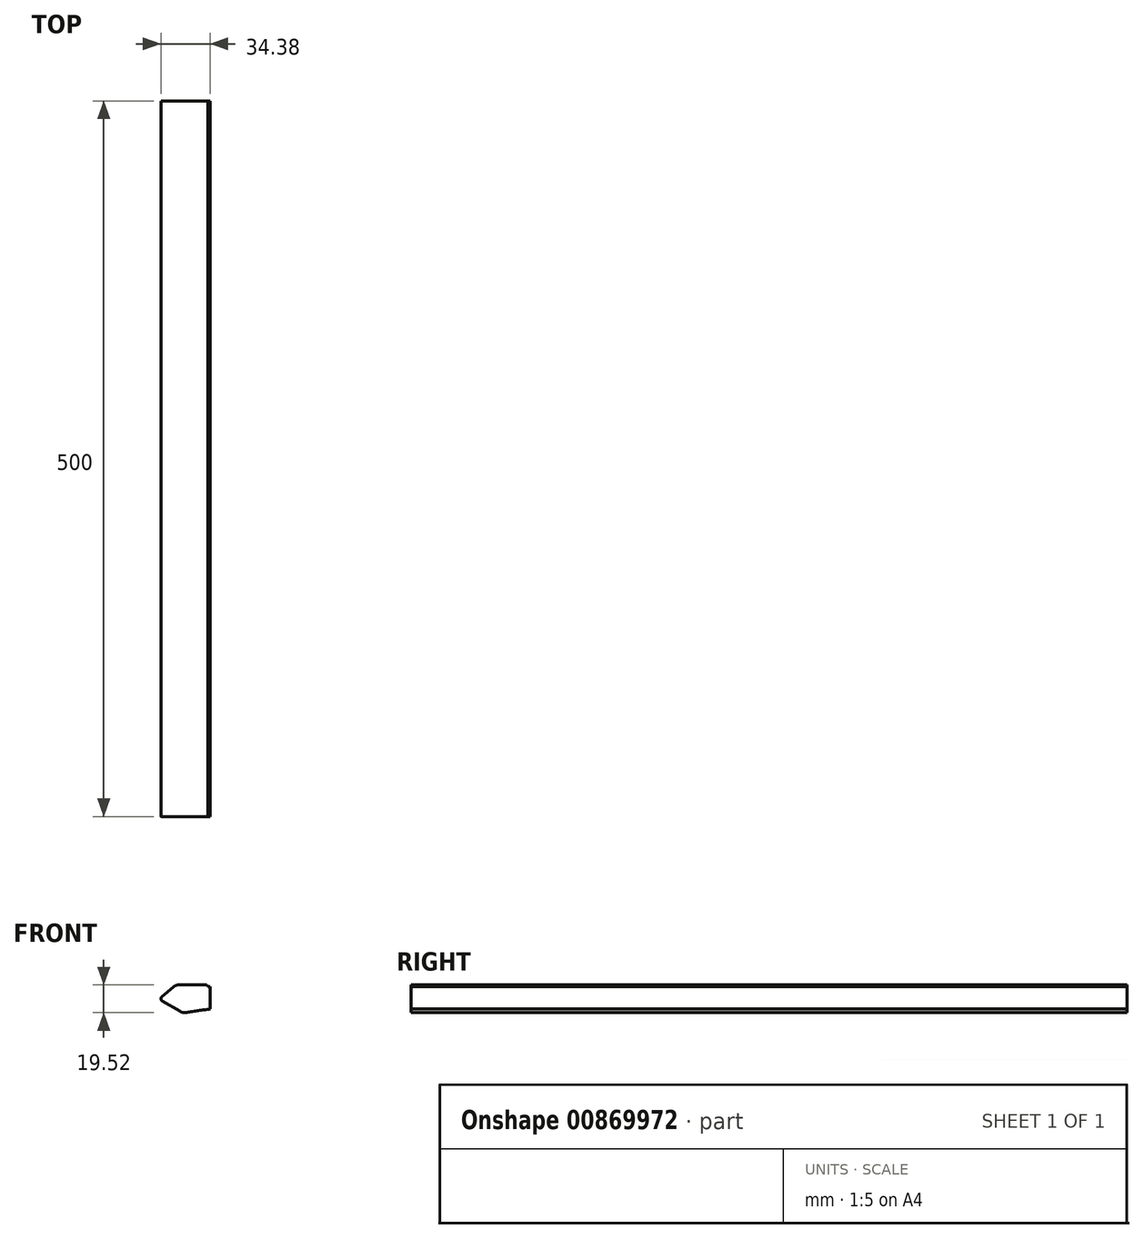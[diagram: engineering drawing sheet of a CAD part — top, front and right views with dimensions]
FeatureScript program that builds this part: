
annotation { "Feature Type Name" : "Feature", "Feature Type Description" : "" }
export const myFeature = defineFeature(function(context is Context, id is Id, definition is map)
    precondition{}
    {
        {
            var Q0;
            Q0=qCreatedBy(makeId("Front.planeOp"),FACE);
            var sketch = newSketch(context, id + "F0", { "sketchPlane" : qUnion([Q0])});
            skLineSegment(sketch, "E0", {"start": v(0, 48.22) * mm, "end": v(0, -32.48) * mm, "construction": true});
            skLineSegment(sketch, "E1", {"start": v(0, 0) * mm, "end": v(22.5, 0) * mm});
            skLineSegment(sketch, "E2", {"start": v(22.5, 0) * mm, "end": v(22.5, 1.3) * mm});
            skLineSegment(sketch, "E3", {"start": v(22.5, 1.3) * mm, "end": v(45.58, 1.3) * mm});
            skLineSegment(sketch, "E4", {"start": v(45.58, 1.3) * mm, "end": v(57.5, -8.7) * mm});
            skLineSegment(sketch, "E5", {"start": v(57.5, -8.7) * mm, "end": v(57.5, -12.7) * mm});
            skLineSegment(sketch, "E6", {"start": v(57.5, -12.7) * mm, "end": v(40.18, -22.7) * mm});
            skLineSegment(sketch, "E7.MirrorCS", {"start": v(0, 0) * mm, "end": v(-22.5, 0) * mm});
            skLineSegment(sketch, "E8.MirrorCS", {"start": v(-22.5, 0) * mm, "end": v(-22.5, 1.3) * mm});
            skLineSegment(sketch, "E9.MirrorCS", {"start": v(-22.5, 1.3) * mm, "end": v(-45.58, 1.3) * mm});
            skLineSegment(sketch, "E10.MirrorCS", {"start": v(-45.58, 1.3) * mm, "end": v(-57.5, -8.7) * mm});
            skLineSegment(sketch, "E11.MirrorCS", {"start": v(-57.5, -8.7) * mm, "end": v(-57.5, -12.7) * mm});
            skLineSegment(sketch, "E12.MirrorCS", {"start": v(-57.5, -12.7) * mm, "end": v(-40.18, -22.7) * mm});
            skArc(sketch, "E13", {"start": v(40.18, -22.7) * mm, "mid": v(0, -18.62) * mm, "end": v(-40.18, -22.7) * mm});
            skSolve(sketch);
        }
        {
            var Q0;
            Q0=makeQuery(id+"F0.imprint","IMPRINT",FACE,{"disambiguationData":[TD([[makeQuery(id+"F0.imprint","IMPRINT",EDGE,{"derivedFrom":sQuery(id+"F0.wireOp",EDGE,"E1")}),-1.0]])]});
            extrude(context, id + "F1", {"entities" : qUnion([Q0]), "endBound" : BoundingType.SYMMETRIC, "depth" : 500 * mm, "offsetDistance" : 25 * mm});
        }
        {
            var Q0;
            Q0=qCreatedBy(makeId("Front.planeOp"),FACE);
            var sketch = newSketch(context, id + "F2", { "sketchPlane" : qUnion([Q0])});
            skLineSegment(sketch, "E14.bottom", {"start": v(-19, -2) * mm, "end": v(19, -2) * mm});
            skLineSegment(sketch, "E14.top", {"start": v(-19, -15) * mm, "end": v(19, -15) * mm});
            skLineSegment(sketch, "E14.left", {"start": v(-19, -2) * mm, "end": v(-19, -15) * mm});
            skLineSegment(sketch, "E14.right", {"start": v(19, -2) * mm, "end": v(19, -15) * mm});
            skSolve(sketch);
        }
        {
            var Q0;
            Q0=qSketchRegion(id+"F2",true);
            extrude(context, id + "F3", {"entities" : qUnion([Q0]), "operationType" : NewBodyOperationType.REMOVE, "endBound" : BoundingType.SYMMETRIC, "oppositeDirection" : true, "depth" : 500 * mm, "offsetDistance" : 25 * mm});
        }
        {
            var Q0;
            Q0=makeQuery(id+"F1.opExtrude","SWEPT_EDGE",EDGE,{"disambiguationData":[OSD([sQuery(id+"F0.wireOp",EDGE,"E2"),sQuery(id+"F0.wireOp",EDGE,"E3")])]});
            var Q1;
            Q1=makeQuery(id+"F1.opExtrude","SWEPT_EDGE",EDGE,{"disambiguationData":[OSD([sQuery(id+"F0.wireOp",EDGE,"E8.MirrorCS"),sQuery(id+"F0.wireOp",EDGE,"E9.MirrorCS")])]});
            fillet(context, id + "F4", {"entities" : qUnion([Q0, Q1]), "radius" : 2 * mm, "tangentPropagation" : true, "allowEdgeOverflow" : false});
        }
        {
            var Q0;
            Q0=makeQuery(id+"F1.opExtrude","SWEPT_EDGE",EDGE,{"disambiguationData":[OSD([sQuery(id+"F0.wireOp",EDGE,"E3"),sQuery(id+"F0.wireOp",EDGE,"E4")])]});
            var Q1;
            Q1=makeQuery(id+"F1.opExtrude","SWEPT_EDGE",EDGE,{"disambiguationData":[OSD([sQuery(id+"F0.wireOp",EDGE,"E9.MirrorCS"),sQuery(id+"F0.wireOp",EDGE,"E10.MirrorCS")])]});
            var Q2;
            Q2=makeQuery(id+"F1.opExtrude","SWEPT_EDGE",EDGE,{"disambiguationData":[OSD([sQuery(id+"F0.wireOp",EDGE,"E6"),sQuery(id+"F0.wireOp",EDGE,"E13")])]});
            var Q3;
            Q3=makeQuery(id+"F1.opExtrude","SWEPT_EDGE",EDGE,{"disambiguationData":[OSD([sQuery(id+"F0.wireOp",EDGE,"E12.MirrorCS"),sQuery(id+"F0.wireOp",EDGE,"E13")])]});
            fillet(context, id + "F5", {"entities" : qUnion([Q0, Q1, Q2, Q3]), "radius" : 9 * mm, "tangentPropagation" : true, "allowEdgeOverflow" : false});
        }
        {
            var Q0;
            Q0=makeQuery(id+"F1.opExtrude","SWEPT_EDGE",EDGE,{"disambiguationData":[OSD([sQuery(id+"F0.wireOp",EDGE,"E4"),sQuery(id+"F0.wireOp",EDGE,"E5")])]});
            var Q1;
            Q1=makeQuery(id+"F1.opExtrude","SWEPT_EDGE",EDGE,{"disambiguationData":[OSD([sQuery(id+"F0.wireOp",EDGE,"E5"),sQuery(id+"F0.wireOp",EDGE,"E6")])]});
            var Q2;
            Q2=makeQuery(id+"F1.opExtrude","SWEPT_EDGE",EDGE,{"disambiguationData":[OSD([sQuery(id+"F0.wireOp",EDGE,"E10.MirrorCS"),sQuery(id+"F0.wireOp",EDGE,"E11.MirrorCS")])]});
            var Q3;
            Q3=makeQuery(id+"F1.opExtrude","SWEPT_EDGE",EDGE,{"disambiguationData":[OSD([sQuery(id+"F0.wireOp",EDGE,"E11.MirrorCS"),sQuery(id+"F0.wireOp",EDGE,"E12.MirrorCS")])]});
            fillet(context, id + "F6", {"entities" : qUnion([Q0, Q1, Q2, Q3]), "radius" : 1 * mm, "tangentPropagation" : true, "allowEdgeOverflow" : false});
        }
        {
            var Q0;
            Q0=qCreatedBy(makeId("Front.planeOp"),FACE);
            var sketch = newSketch(context, id + "F7", { "sketchPlane" : qUnion([Q0])});
            skLineSegment(sketch, "E15.0.0", {"start": v(43.1, -21.01) * mm, "end": v(57, -12.99) * mm});
            skArc(sketch, "E15.0.1", {"start": v(57, -12.99) * mm, "mid": v(57.37, -12.62) * mm, "end": v(57.5, -12.12) * mm});
            skLineSegment(sketch, "E15.0.2", {"start": v(57.5, -12.12) * mm, "end": v(57.5, -9.17) * mm});
            skArc(sketch, "E15.0.3", {"start": v(57.5, -9.17) * mm, "mid": v(57.4, -8.74) * mm, "end": v(57.14, -8.4) * mm});
            skLineSegment(sketch, "E15.0.4", {"start": v(57.14, -8.4) * mm, "end": v(48.1, -0.8) * mm});
            skArc(sketch, "E15.0.5", {"start": v(48.1, -0.8) * mm, "mid": v(45.38, 0.76) * mm, "end": v(42.3, 1.3) * mm});
            skLineSegment(sketch, "E15.0.6", {"start": v(42.3, 1.3) * mm, "end": v(24.37, 1.3) * mm});
            skArc(sketch, "E15.0.7", {"start": v(24.37, 1.3) * mm, "mid": v(23.23, 0.94) * mm, "end": v(22.5, 0) * mm});
            skLineSegment(sketch, "E15.0.8", {"start": v(22.5, 0) * mm, "end": v(-22.5, 0) * mm});
            skArc(sketch, "E15.0.9", {"start": v(-22.5, 0) * mm, "mid": v(-23.23, 0.94) * mm, "end": v(-24.37, 1.3) * mm});
            skLineSegment(sketch, "E15.0.10", {"start": v(-24.37, 1.3) * mm, "end": v(-42.3, 1.3) * mm});
            skArc(sketch, "E15.0.11", {"start": v(-42.3, 1.3) * mm, "mid": v(-45.38, 0.76) * mm, "end": v(-48.1, -0.8) * mm});
            skLineSegment(sketch, "E15.0.12", {"start": v(-48.1, -0.8) * mm, "end": v(-57.14, -8.4) * mm});
            skArc(sketch, "E15.0.13", {"start": v(-57.14, -8.4) * mm, "mid": v(-57.4, -8.74) * mm, "end": v(-57.5, -9.17) * mm});
            skLineSegment(sketch, "E15.0.14", {"start": v(-57.5, -9.17) * mm, "end": v(-57.5, -12.12) * mm});
            skArc(sketch, "E15.0.15", {"start": v(-57.5, -12.12) * mm, "mid": v(-57.37, -12.62) * mm, "end": v(-57, -12.99) * mm});
            skLineSegment(sketch, "E15.0.16", {"start": v(-57, -12.99) * mm, "end": v(-43.1, -21.01) * mm});
            skArc(sketch, "E15.0.17", {"start": v(-43.1, -21.01) * mm, "mid": v(-40.12, -22.1) * mm, "end": v(-36.94, -22.06) * mm});
            skArc(sketch, "E15.0.18", {"start": v(-36.94, -22.06) * mm, "mid": v(0, -18.62) * mm, "end": v(36.94, -22.06) * mm});
            skArc(sketch, "E15.0.19", {"start": v(36.94, -22.06) * mm, "mid": v(40.12, -22.1) * mm, "end": v(43.1, -21.01) * mm});
            skArc(sketch, "E16.0", {"start": v(-37.3, -20.1) * mm, "mid": v(-29.18, -18.74) * mm, "end": v(-21, -17.72) * mm});
            skArc(sketch, "E16.1", {"start": v(-42.1, -19.28) * mm, "mid": v(-39.78, -20.12) * mm, "end": v(-37.3, -20.1) * mm});
            skLineSegment(sketch, "E16.2", {"start": v(-24.37, -0.7) * mm, "end": v(-42.3, -0.7) * mm});
            skArc(sketch, "E16.3", {"start": v(-42.3, -0.7) * mm, "mid": v(-44.7, -1.12) * mm, "end": v(-46.8, -2.34) * mm});
            skLineSegment(sketch, "E16.4", {"start": v(-46.8, -2.34) * mm, "end": v(-54.66, -8.93) * mm});
            skLineSegment(sketch, "E16.5", {"start": v(-54.38, -12.2) * mm, "end": v(-42.1, -19.28) * mm});
            skPoint(sketch, "E17.visualSharp", {"position": v(-56.85, -10.77) * mm});
            skArc(sketch, "E17.filletArc", {"start": v(-54.66, -8.93) * mm, "mid": v(-55.37, -10.64) * mm, "end": v(-54.38, -12.2) * mm});
            skLineSegment(sketch, "E18.0", {"start": v(-21, -2) * mm, "end": v(-21, -17.72) * mm});
            skLineSegment(sketch, "E19.0", {"start": v(-21, -2) * mm, "end": v(-22.5, -2) * mm});
            skArc(sketch, "E20", {"start": v(-22.5, -2) * mm, "mid": v(-23.23, -1.06) * mm, "end": v(-24.37, -0.7) * mm});
            skLineSegment(sketch, "E21", {"start": v(0, 15.86) * mm, "end": v(0, -28.92) * mm, "construction": true});
            skLineSegment(sketch, "E22.MirrorCS", {"start": v(24.37, -0.7) * mm, "end": v(42.3, -0.7) * mm});
            skArc(sketch, "E23.MirrorCS", {"start": v(42.3, -0.7) * mm, "mid": v(44.7, -1.12) * mm, "end": v(46.8, -2.34) * mm});
            skLineSegment(sketch, "E24.MirrorCS", {"start": v(46.8, -2.34) * mm, "end": v(54.66, -8.93) * mm});
            skArc(sketch, "E25.MirrorCS", {"start": v(54.66, -8.93) * mm, "mid": v(55.37, -10.64) * mm, "end": v(54.38, -12.2) * mm});
            skLineSegment(sketch, "E26.MirrorCS", {"start": v(54.38, -12.2) * mm, "end": v(42.1, -19.28) * mm});
            skArc(sketch, "E27.MirrorCS", {"start": v(42.1, -19.28) * mm, "mid": v(39.78, -20.12) * mm, "end": v(37.3, -20.1) * mm});
            skArc(sketch, "E28.MirrorCS", {"start": v(37.3, -20.1) * mm, "mid": v(29.18, -18.74) * mm, "end": v(21, -17.72) * mm});
            skLineSegment(sketch, "E29.MirrorCS", {"start": v(21, -2) * mm, "end": v(21, -17.72) * mm});
            skLineSegment(sketch, "E30.MirrorCS", {"start": v(21, -2) * mm, "end": v(22.5, -2) * mm});
            skArc(sketch, "E31.MirrorCS", {"start": v(22.5, -2) * mm, "mid": v(23.23, -1.06) * mm, "end": v(24.37, -0.7) * mm});
            skSolve(sketch);
        }
        {
            var Q0;
            Q0=makeQuery(id+"F7.imprint","IMPRINT",FACE,{"disambiguationData":[TD([[makeQuery(id+"F7.imprint","IMPRINT",EDGE,{"derivedFrom":sQuery(id+"F7.wireOp",EDGE,"E16.0")}),1.0]])]});
            var Q1;
            Q1=makeQuery(id+"F7.imprint","IMPRINT",FACE,{"disambiguationData":[TD([[makeQuery(id+"F7.imprint","IMPRINT",EDGE,{"derivedFrom":sQuery(id+"F7.wireOp",EDGE,"E22.MirrorCS")}),-1.0]])]});
            extrude(context, id + "F8", {"entities" : qUnion([Q0, Q1]), "operationType" : NewBodyOperationType.REMOVE, "endBound" : BoundingType.SYMMETRIC, "oppositeDirection" : true, "depth" : 500 * mm, "offsetDistance" : 25 * mm});
        }
    });
